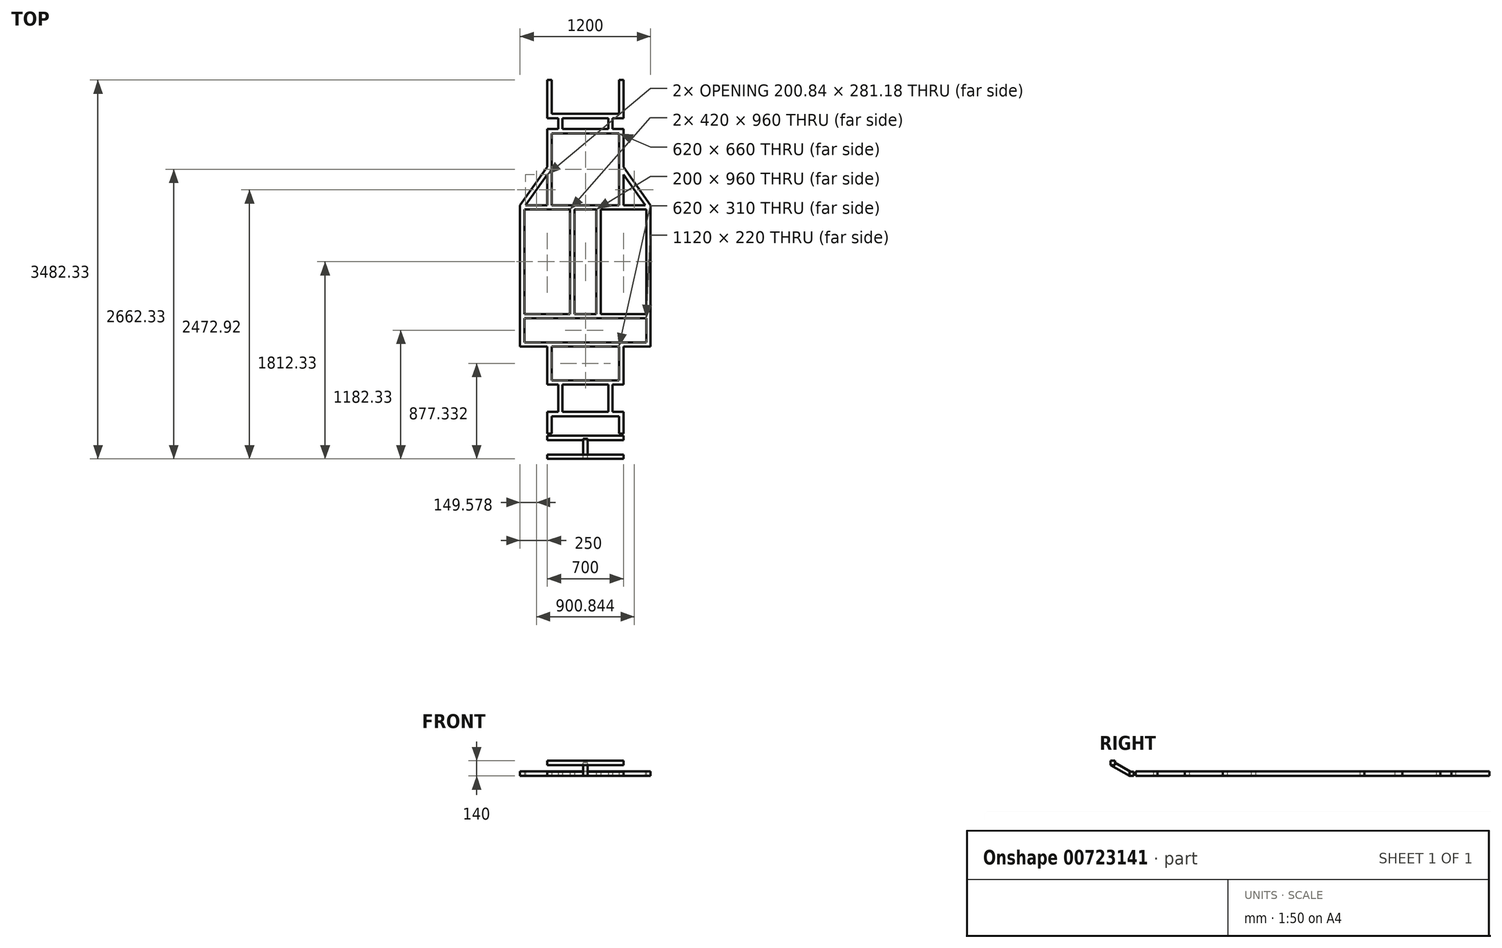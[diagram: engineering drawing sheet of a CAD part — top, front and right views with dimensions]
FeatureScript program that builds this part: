
annotation { "Feature Type Name" : "Feature", "Feature Type Description" : "" }
export const myFeature = defineFeature(function(context is Context, id is Id, definition is map)
    precondition{}
    {
        {
            var Q0;
            Q0=qCreatedBy(makeId("Top.planeOp"),FACE);
            var sketch = newSketch(context, id + "F0", { "sketchPlane" : qUnion([Q0])});
            skLineSegment(sketch, "E0.bottom", {"start": v(-100, -560.39) * mm, "end": v(100, -560.39) * mm});
            skLineSegment(sketch, "E0.top", {"start": v(-100, 439.61) * mm, "end": v(100, 439.61) * mm});
            skLineSegment(sketch, "E0.right", {"start": v(100, -560.39) * mm, "end": v(100, 399.61) * mm});
            skPoint(sketch, "E0.middle", {"position": v(0, -60.39) * mm});
            skLineSegment(sketch, "E1.bottom", {"start": v(-140, -560.39) * mm, "end": v(-600, -560.39) * mm});
            skLineSegment(sketch, "E1.top", {"start": v(-100, 439.61) * mm, "end": v(-310, 439.61) * mm});
            skLineSegment(sketch, "E1.right", {"start": v(-600, -560.39) * mm, "end": v(-600, 439.61) * mm});
            skLineSegment(sketch, "E2.bottom", {"start": v(140, -560.39) * mm, "end": v(560, -560.39) * mm});
            skLineSegment(sketch, "E2.top", {"start": v(100, 439.61) * mm, "end": v(550.84, 439.61) * mm});
            skLineSegment(sketch, "E2.right", {"start": v(600, -560.39) * mm, "end": v(600, 439.61) * mm});
            skLineSegment(sketch, "E3.bottom", {"start": v(560, -560.39) * mm, "end": v(140, -560.39) * mm});
            skLineSegment(sketch, "E3.top", {"start": v(600, -860.39) * mm, "end": v(350, -860.39) * mm});
            skLineSegment(sketch, "E3.left", {"start": v(600, -560.39) * mm, "end": v(600, -860.39) * mm});
            skLineSegment(sketch, "E3.right", {"start": v(-600, -560.39) * mm, "end": v(-600, -860.39) * mm});
            skPoint(sketch, "E4.oppositeSnap0", {"position": v(350, 439.61) * mm});
            skLineSegment(sketch, "E4.bottom", {"start": v(0, 439.61) * mm, "end": v(350, 439.61) * mm});
            skLineSegment(sketch, "E4.top", {"start": v(0, 1139.61) * mm, "end": v(350, 1139.61) * mm});
            skLineSegment(sketch, "E4.right", {"start": v(350, 439.61) * mm, "end": v(350, 720.8) * mm});
            skLineSegment(sketch, "E5.bottom", {"start": v(0, 439.61) * mm, "end": v(-310, 439.61) * mm});
            skLineSegment(sketch, "E5.top", {"start": v(0, 1139.61) * mm, "end": v(-210, 1139.61) * mm});
            skLineSegment(sketch, "E5.right", {"start": v(-350, 439.61) * mm, "end": v(-350, 720.8) * mm});
            skLineSegment(sketch, "E6", {"start": v(600, 439.61) * mm, "end": v(350, 789.61) * mm});
            skLineSegment(sketch, "E7", {"start": v(350, 789.61) * mm, "end": v(310, 789.61) * mm});
            skLineSegment(sketch, "E8", {"start": v(-350, 789.61) * mm, "end": v(-600, 439.61) * mm});
            skLineSegment(sketch, "E9.bottom", {"start": v(0, 1139.61) * mm, "end": v(250, 1139.61) * mm});
            skLineSegment(sketch, "E9.top", {"start": v(0, 1239.61) * mm, "end": v(250, 1239.61) * mm});
            skLineSegment(sketch, "E9.right", {"start": v(250, 1139.61) * mm, "end": v(250, 1239.61) * mm});
            skLineSegment(sketch, "E10.bottom", {"start": v(0, 1139.61) * mm, "end": v(-250, 1139.61) * mm});
            skLineSegment(sketch, "E10.top", {"start": v(0, 1239.61) * mm, "end": v(-250, 1239.61) * mm});
            skLineSegment(sketch, "E10.left", {"start": v(0, 1139.61) * mm, "end": v(0, 1239.61) * mm});
            skLineSegment(sketch, "E10.right", {"start": v(-250, 1139.61) * mm, "end": v(-250, 1239.61) * mm});
            skLineSegment(sketch, "E11.bottom", {"start": v(0, 1239.61) * mm, "end": v(350, 1239.61) * mm});
            skLineSegment(sketch, "E11.top", {"start": v(310, 1589.61) * mm, "end": v(350, 1589.61) * mm});
            skLineSegment(sketch, "E11.right", {"start": v(350, 1239.61) * mm, "end": v(350, 1589.61) * mm});
            skLineSegment(sketch, "E12.bottom", {"start": v(0, 1239.61) * mm, "end": v(-350, 1239.61) * mm});
            skLineSegment(sketch, "E12.top", {"start": v(-310, 1589.61) * mm, "end": v(-350, 1589.61) * mm});
            skLineSegment(sketch, "E12.right", {"start": v(-350, 1239.61) * mm, "end": v(-350, 1589.61) * mm});
            skLineSegment(sketch, "E13.top", {"start": v(0, -1460.39) * mm, "end": v(210, -1460.39) * mm});
            skLineSegment(sketch, "E14.top", {"start": v(0, -1210.39) * mm, "end": v(210, -1210.39) * mm});
            skLineSegment(sketch, "E14.right", {"start": v(250, -1460.39) * mm, "end": v(250, -1210.39) * mm});
            skLineSegment(sketch, "E15.bottom", {"start": v(0, -1460.39) * mm, "end": v(-210, -1460.39) * mm});
            skLineSegment(sketch, "E15.top", {"start": v(0, -1210.39) * mm, "end": v(-210, -1210.39) * mm});
            skLineSegment(sketch, "E15.right", {"start": v(-250, -1460.39) * mm, "end": v(-250, -1210.39) * mm});
            skLineSegment(sketch, "E16", {"start": v(250, -1210.39) * mm, "end": v(350, -1210.39) * mm});
            skLineSegment(sketch, "E17", {"start": v(-250, -1210.39) * mm, "end": v(-350, -1210.39) * mm});
            skLineSegment(sketch, "E18.bottom", {"start": v(350, -1460.39) * mm, "end": v(250, -1460.39) * mm});
            skLineSegment(sketch, "E18.left", {"start": v(350, -1460.39) * mm, "end": v(350, -1660.39) * mm});
            skLineSegment(sketch, "E18.right", {"start": v(-350, -1460.39) * mm, "end": v(-350, -1660.39) * mm});
            skLineSegment(sketch, "E19", {"start": v(350, -1210.39) * mm, "end": v(350, -860.39) * mm});
            skLineSegment(sketch, "E20", {"start": v(-350, -1210.39) * mm, "end": v(-350, -860.39) * mm});
            skLineSegment(sketch, "E21.0", {"start": v(-310, -1500.39) * mm, "end": v(-310, -1660.39) * mm});
            skLineSegment(sketch, "E22.0", {"start": v(310, -1500.39) * mm, "end": v(310, -1660.39) * mm});
            skLineSegment(sketch, "E23.0", {"start": v(210, -1460.39) * mm, "end": v(210, -1210.39) * mm});
            skLineSegment(sketch, "E24.0", {"start": v(-210, -1460.39) * mm, "end": v(-210, -1210.39) * mm});
            skLineSegment(sketch, "E25.0", {"start": v(-310, -1212.96) * mm, "end": v(-310, -1210.39) * mm});
            skLineSegment(sketch, "E26.0", {"start": v(310, -1170.39) * mm, "end": v(310, -860.39) * mm});
            skLineSegment(sketch, "E27.0", {"start": v(310, 439.61) * mm, "end": v(310, 1099.61) * mm});
            skLineSegment(sketch, "E28.0", {"start": v(-310, 439.61) * mm, "end": v(-310, 1099.61) * mm});
            skLineSegment(sketch, "E29.0", {"start": v(210, 1139.61) * mm, "end": v(210, 1239.61) * mm});
            skLineSegment(sketch, "E30.0", {"start": v(-210, 1139.61) * mm, "end": v(-210, 1239.61) * mm});
            skLineSegment(sketch, "E31.0", {"start": v(-310, 1239.61) * mm, "end": v(-310, 1589.61) * mm});
            skLineSegment(sketch, "E32.0", {"start": v(310, 1239.61) * mm, "end": v(310, 1589.61) * mm});
            skLineSegment(sketch, "E33.trimOffspring", {"start": v(-310, 789.61) * mm, "end": v(-350, 789.61) * mm});
            skLineSegment(sketch, "E34.0", {"start": v(140, 399.61) * mm, "end": v(560, 399.61) * mm});
            skLineSegment(sketch, "E35.0", {"start": v(-140, 399.61) * mm, "end": v(-560, 399.61) * mm});
            skLineSegment(sketch, "E36.0", {"start": v(-100, 399.61) * mm, "end": v(100, 399.61) * mm});
            skLineSegment(sketch, "E37.0", {"start": v(-350, 720.8) * mm, "end": v(-550.84, 439.61) * mm});
            skLineSegment(sketch, "E38.0", {"start": v(550.84, 439.61) * mm, "end": v(350, 720.8) * mm});
            skLineSegment(sketch, "E39.0", {"start": v(0, 1099.61) * mm, "end": v(310, 1099.61) * mm});
            skLineSegment(sketch, "E39.1", {"start": v(0, 1099.61) * mm, "end": v(-310, 1099.61) * mm});
            skLineSegment(sketch, "E40.0", {"start": v(0, 1279.61) * mm, "end": v(-350, 1279.61) * mm});
            skLineSegment(sketch, "E40.1", {"start": v(0, 1279.61) * mm, "end": v(350, 1279.61) * mm});
            skLineSegment(sketch, "E41.0", {"start": v(560, -560.39) * mm, "end": v(560, 399.61) * mm});
            skLineSegment(sketch, "E41.1", {"start": v(560, -600.39) * mm, "end": v(560, -820.39) * mm});
            skLineSegment(sketch, "E42.0", {"start": v(-560, -560.39) * mm, "end": v(-560, 399.61) * mm});
            skLineSegment(sketch, "E43.0", {"start": v(-560, -600.39) * mm, "end": v(-560, -820.39) * mm});
            skLineSegment(sketch, "E44.0", {"start": v(560, -820.39) * mm, "end": v(-560, -820.39) * mm});
            skLineSegment(sketch, "E45.0", {"start": v(-140, -560.39) * mm, "end": v(-140, 399.61) * mm});
            skLineSegment(sketch, "E46.0", {"start": v(140, -560.39) * mm, "end": v(140, 399.61) * mm});
            skLineSegment(sketch, "E47.0", {"start": v(560, -600.39) * mm, "end": v(-560, -600.39) * mm});
            skLineSegment(sketch, "E48.trimOffspring", {"start": v(-140, -560.39) * mm, "end": v(-560, -560.39) * mm});
            skLineSegment(sketch, "E49.trimOffspring", {"start": v(100, -560.39) * mm, "end": v(-100, -560.39) * mm});
            skLineSegment(sketch, "E50", {"start": v(-100, -560.39) * mm, "end": v(-100, 399.61) * mm});
            skLineSegment(sketch, "E51.bottom", {"start": v(310, -1210.39) * mm, "end": v(250, -1210.39) * mm});
            skLineSegment(sketch, "E51.top", {"start": v(310, -1170.39) * mm, "end": v(-310, -1170.39) * mm});
            skLineSegment(sketch, "E52.bottom", {"start": v(310, -1460.39) * mm, "end": v(250, -1460.39) * mm});
            skLineSegment(sketch, "E52.top", {"start": v(310, -1500.39) * mm, "end": v(-310, -1500.39) * mm});
            skLineSegment(sketch, "E53.trimOffspring", {"start": v(-350, 439.61) * mm, "end": v(-550.84, 439.61) * mm});
            skLineSegment(sketch, "E54.trimOffspring", {"start": v(-350, 789.61) * mm, "end": v(-350, 1139.61) * mm});
            skLineSegment(sketch, "E55.trimOffspring", {"start": v(350, 789.61) * mm, "end": v(350, 1139.61) * mm});
            skLineSegment(sketch, "E56.trimOffspring", {"start": v(-250, 1139.61) * mm, "end": v(-350, 1139.61) * mm});
            skLineSegment(sketch, "E57.trimOffspring", {"start": v(-350, -860.39) * mm, "end": v(-600, -860.39) * mm});
            skPoint(sketch, "E13.bottom.start.orphan", {"position": v(0, -860.39) * mm});
            skLineSegment(sketch, "E58.trimOffspring", {"start": v(-310, -1170.39) * mm, "end": v(-310, -860.39) * mm});
            skLineSegment(sketch, "E59.trimOffspring", {"start": v(210, -1210.39) * mm, "end": v(-210, -1210.39) * mm});
            skLineSegment(sketch, "E60.trimOffspring", {"start": v(-250, -1210.39) * mm, "end": v(-310, -1210.39) * mm});
            skLineSegment(sketch, "E61", {"start": v(310, -860.39) * mm, "end": v(-310, -860.39) * mm});
            skLineSegment(sketch, "E62.trimOffspring", {"start": v(-250, -1460.39) * mm, "end": v(-350, -1460.39) * mm});
            skLineSegment(sketch, "E63.trimOffspring", {"start": v(-250, -1460.39) * mm, "end": v(-310, -1460.39) * mm});
            skLineSegment(sketch, "E64.trimOffspring", {"start": v(210, -1460.39) * mm, "end": v(-210, -1460.39) * mm});
            skLineSegment(sketch, "E65.trimOffspring", {"start": v(250, -1460.39) * mm, "end": v(350, -1460.39) * mm});
            skLineSegment(sketch, "E66", {"start": v(350, -1660.39) * mm, "end": v(310, -1660.39) * mm});
            skLineSegment(sketch, "E67", {"start": v(-310, -1660.39) * mm, "end": v(-350, -1660.39) * mm});
            skSolve(sketch);
        }
        {
            var Q0;
            Q0 = qSketchRegion(id + "F0", true);
            extrude(context, id + "F1", {"entities" : qUnion([Q0]), "endBound" : BoundingType.SYMMETRIC, "depth" : 40 * mm, "offsetDistance" : 25 * mm});
        }
        {
            var Q0;
            Q0=qCreatedBy(makeId("Right.planeOp"),FACE);
            var sketch = newSketch(context, id + "F2", { "sketchPlane" : qUnion([Q0])});
            skLineSegment(sketch, "E68.bottom", {"start": v(-1679.51, 19) * mm, "end": v(-1719.51, 19) * mm});
            skLineSegment(sketch, "E68.top", {"start": v(-1679.51, -21) * mm, "end": v(-1719.51, -21) * mm});
            skLineSegment(sketch, "E68.left", {"start": v(-1679.51, 19) * mm, "end": v(-1679.51, -21) * mm});
            skLineSegment(sketch, "E68.right", {"start": v(-1719.51, 19) * mm, "end": v(-1719.51, -21) * mm});
            skLineSegment(sketch, "E69", {"start": v(-1719.51, -21) * mm, "end": v(-1892.72, 79) * mm});
            skLineSegment(sketch, "E70.bottom", {"start": v(-1892.72, 79) * mm, "end": v(-1852.72, 79) * mm});
            skLineSegment(sketch, "E70.top", {"start": v(-1892.72, 119) * mm, "end": v(-1852.72, 119) * mm});
            skLineSegment(sketch, "E70.left", {"start": v(-1892.72, 79) * mm, "end": v(-1892.72, 119) * mm});
            skLineSegment(sketch, "E70.right", {"start": v(-1852.72, 79) * mm, "end": v(-1852.72, 119) * mm});
            skLineSegment(sketch, "E71.0", {"start": v(-1708.8, 19) * mm, "end": v(-1852.72, 102.1) * mm});
            skSolve(sketch);
        }
        {
            var Q0;
            {var subQ0=sQuery(id+"F2.wireOp",EDGE,"E68.right");Q0=makeQuery(id+"F2.imprint","IMPRINT",FACE,{"disambiguationData":[TD([[makeQuery(id+"F2.imprint","IMPRINT",EDGE,{"derivedFrom":subQ0}),-1.0]])]});}
            extrude(context, id + "F3", {"entities" : qUnion([Q0]), "endBound" : BoundingType.SYMMETRIC, "depth" : 40 * mm, "offsetDistance" : 25 * mm});
        }
        {
            var Q0;
            {var subQ1=sQuery(id+"F2.wireOp",EDGE,"E70.bottom");Q0=makeQuery(id+"F2.imprint","IMPRINT",FACE,{"disambiguationData":[TD([[makeQuery(id+"F2.imprint","IMPRINT",EDGE,{"derivedFrom":subQ1}),1.0]])]});}
            var Q1;
            Q1=makeQuery(id+"F2.imprint","IMPRINT",FACE,{"disambiguationData":[TD([[makeQuery(id+"F2.imprint","IMPRINT",EDGE,{"derivedFrom":sQuery(id+"F2.wireOp",EDGE,"E68.top")}),-1.0]])]});
            extrude(context, id + "F4", {"entities" : qUnion([Q0, Q1]), "operationType" : NewBodyOperationType.ADD, "endBound" : BoundingType.SYMMETRIC, "depth" : 700 * mm, "offsetDistance" : 25 * mm});
        }
    });
